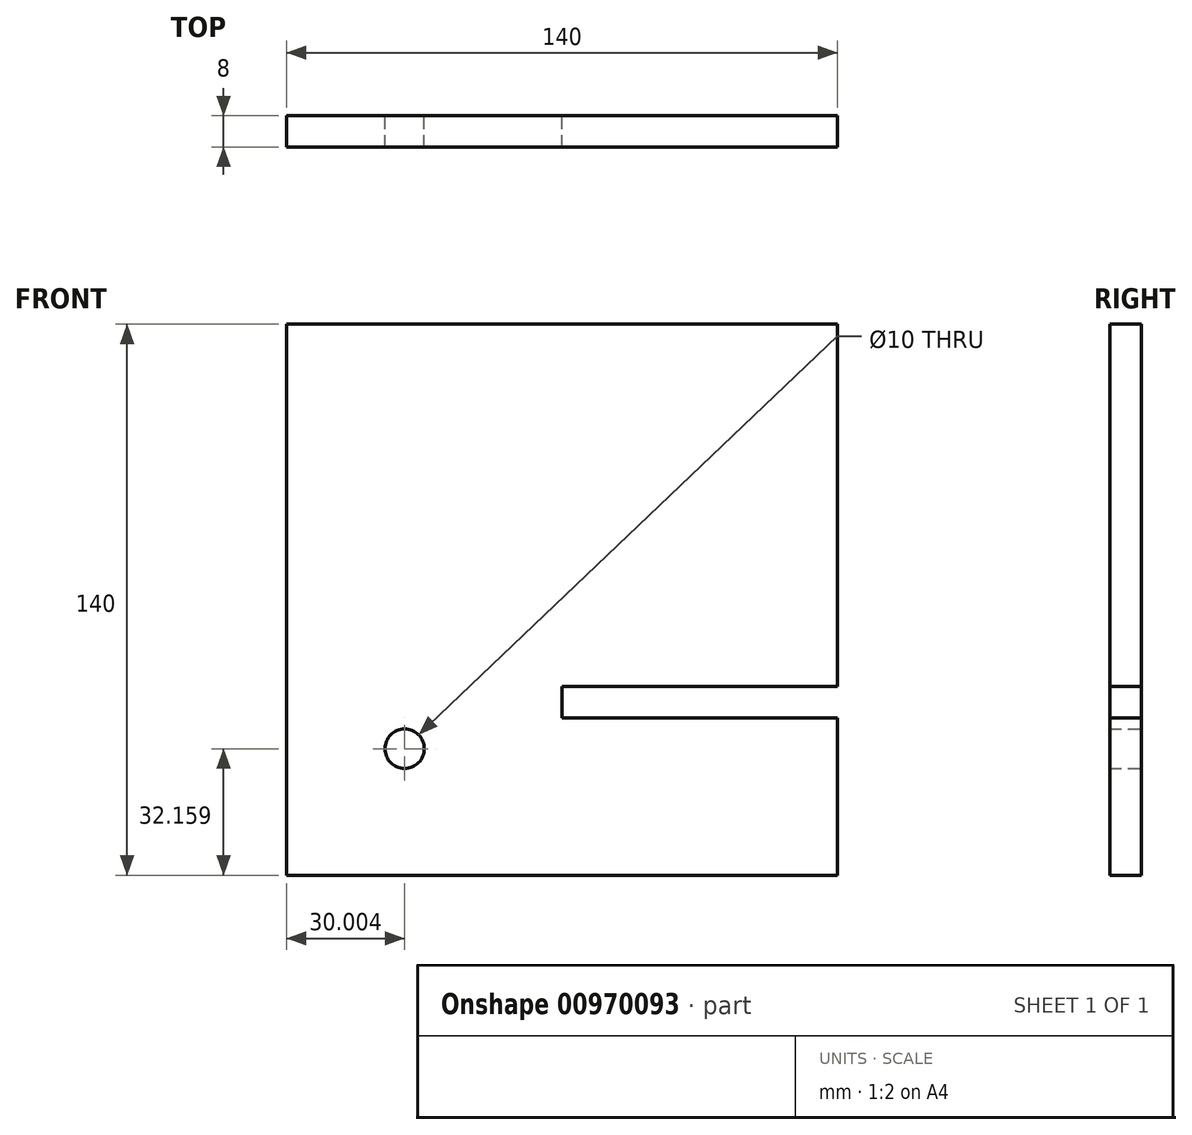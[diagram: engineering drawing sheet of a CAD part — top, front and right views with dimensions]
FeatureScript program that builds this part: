
annotation { "Feature Type Name" : "Feature", "Feature Type Description" : "" }
export const myFeature = defineFeature(function(context is Context, id is Id, definition is map)
    precondition{}
    {
        {
            var Q0;
            Q0=qCreatedBy(makeId("Front.planeOp"),FACE);
            var sketch = newSketch(context, id + "F0", { "sketchPlane" : qUnion([Q0])});
            skLineSegment(sketch, "E0.bottom", {"start": v(-99.09, 135.73) * mm, "end": v(40.91, 135.73) * mm});
            skLineSegment(sketch, "E0.top", {"start": v(-99.09, -4.27) * mm, "end": v(40.91, -4.27) * mm});
            skLineSegment(sketch, "E0.left", {"start": v(-99.09, 135.73) * mm, "end": v(-99.09, -4.27) * mm});
            skLineSegment(sketch, "E0.right", {"start": v(40.91, 135.73) * mm, "end": v(40.91, 43.73) * mm});
            skLineSegment(sketch, "E1", {"start": v(40.91, 43.73) * mm, "end": v(-29.09, 43.73) * mm});
            skLineSegment(sketch, "E2", {"start": v(-29.09, 43.73) * mm, "end": v(-29.09, 35.73) * mm});
            skLineSegment(sketch, "E3", {"start": v(-29.09, 35.73) * mm, "end": v(40.91, 35.73) * mm});
            skLineSegment(sketch, "E4.trimOffspring", {"start": v(40.91, 35.73) * mm, "end": v(40.91, -4.27) * mm});
            skCircle(sketch, "E5", {"center": v(-69.09, 27.89) * mm, "radius": 5 * mm});
            skSolve(sketch);
        }
        {
            var Q0;
            Q0 = qSketchRegion(id + "F0", true);
            extrude(context, id + "F1", {"entities" : qUnion([Q0]), "depth" : 8 * mm, "offsetDistance" : 25 * mm});
        }
    });
